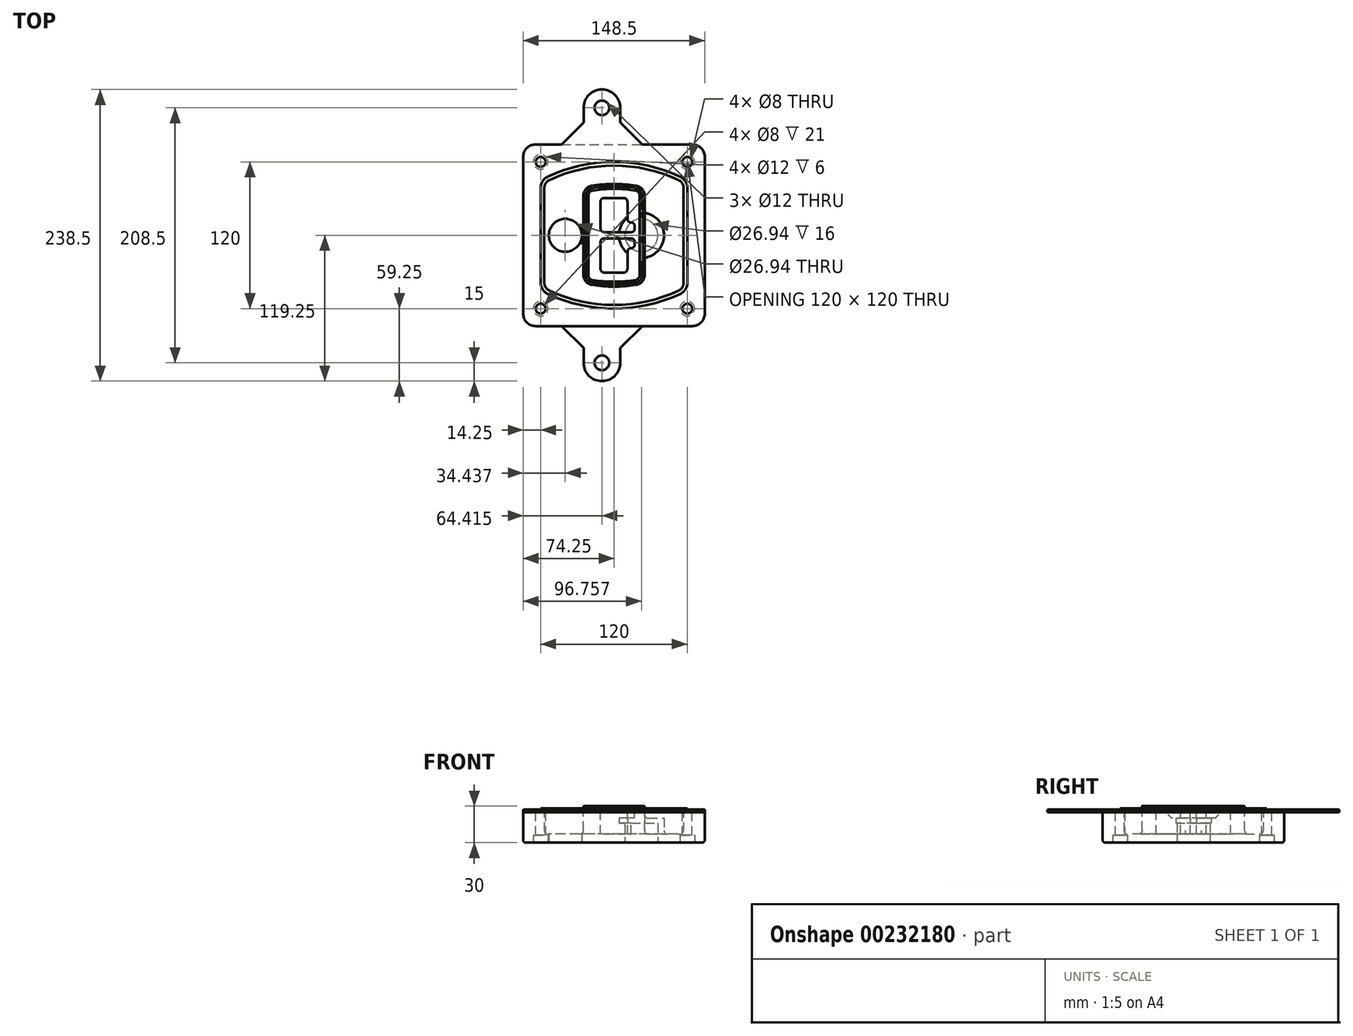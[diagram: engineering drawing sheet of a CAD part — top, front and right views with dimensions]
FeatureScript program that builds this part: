
annotation { "Feature Type Name" : "Feature", "Feature Type Description" : "" }
export const myFeature = defineFeature(function(context is Context, id is Id, definition is map)
    precondition{}
    {
        {
            var Q0;
            Q0=qCreatedBy(makeId("Top.planeOp"),FACE);
            var sketch = newSketch(context, id + "F0", { "sketchPlane" : qUnion([Q0])});
            skPoint(sketch, "E0.rect.middle", {"position": v(0, 0) * mm});
            skLineSegment(sketch, "E1.bottom", {"start": v(-64.25, -74.25) * mm, "end": v(64.25, -74.25) * mm});
            skLineSegment(sketch, "E1.top", {"start": v(-64.25, 74.25) * mm, "end": v(64.25, 74.25) * mm});
            skLineSegment(sketch, "E1.left", {"start": v(-74.25, -64.25) * mm, "end": v(-74.25, 64.25) * mm});
            skLineSegment(sketch, "E1.right", {"start": v(74.25, -64.25) * mm, "end": v(74.25, 64.25) * mm});
            skLineSegment(sketch, "E2", {"start": v(-74.25, 74.25) * mm, "end": v(74.25, -74.25) * mm, "construction": true});
            skLineSegment(sketch, "E3", {"start": v(74.25, 74.25) * mm, "end": v(-74.25, -74.25) * mm, "construction": true});
            skCircle(sketch, "E4", {"center": v(-60, 60) * mm, "radius": 4 * mm});
            skCircle(sketch, "E5", {"center": v(60, 60) * mm, "radius": 4 * mm});
            skCircle(sketch, "E6", {"center": v(60, -60) * mm, "radius": 4 * mm});
            skCircle(sketch, "E7", {"center": v(-60, -60) * mm, "radius": 4 * mm});
            skLineSegment(sketch, "E8", {"start": v(-60, 60) * mm, "end": v(60, 60) * mm, "construction": true});
            skLineSegment(sketch, "E9", {"start": v(60, 60) * mm, "end": v(60, -60) * mm, "construction": true});
            skLineSegment(sketch, "E10", {"start": v(60, -60) * mm, "end": v(-60, -60) * mm, "construction": true});
            skLineSegment(sketch, "E11", {"start": v(-60, -60) * mm, "end": v(-60, 60) * mm, "construction": true});
            skLineSegment(sketch, "E12", {"start": v(-60, 38.83) * mm, "end": v(-60, -38.83) * mm});
            skLineSegment(sketch, "E13", {"start": v(60, 38.83) * mm, "end": v(60, -38.83) * mm});
            skArc(sketch, "E14", {"start": v(54.26, 47.88) * mm, "mid": v(0, 60) * mm, "end": v(-54.26, 47.88) * mm});
            skArc(sketch, "E15", {"start": v(-54.26, -47.88) * mm, "mid": v(0, -60) * mm, "end": v(54.26, -47.88) * mm});
            skLineSegment(sketch, "E16", {"start": v(-60, 0) * mm, "end": v(60, 0) * mm, "construction": true});
            skPoint(sketch, "E17.visualSharp", {"position": v(-60, -45) * mm});
            skArc(sketch, "E17.filletArc", {"start": v(-60, -38.83) * mm, "mid": v(-58.44, -44.2) * mm, "end": v(-54.26, -47.88) * mm});
            skPoint(sketch, "E18.visualSharp", {"position": v(-60, 45) * mm});
            skArc(sketch, "E18.filletArc", {"start": v(-54.26, 47.88) * mm, "mid": v(-58.44, 44.2) * mm, "end": v(-60, 38.83) * mm});
            skPoint(sketch, "E19.visualSharp", {"position": v(60, 45) * mm});
            skArc(sketch, "E19.filletArc", {"start": v(60, 38.83) * mm, "mid": v(58.44, 44.2) * mm, "end": v(54.26, 47.88) * mm});
            skPoint(sketch, "E20.visualSharp", {"position": v(60, -45) * mm});
            skArc(sketch, "E20.filletArc", {"start": v(54.26, -47.88) * mm, "mid": v(58.44, -44.2) * mm, "end": v(60, -38.83) * mm});
            skPoint(sketch, "E21.visualSharp", {"position": v(-74.25, 74.25) * mm});
            skArc(sketch, "E21.filletArc", {"start": v(-64.25, 74.25) * mm, "mid": v(-71.32, 71.32) * mm, "end": v(-74.25, 64.25) * mm});
            skPoint(sketch, "E22.visualSharp", {"position": v(74.25, 74.25) * mm});
            skArc(sketch, "E22.filletArc", {"start": v(74.25, 64.25) * mm, "mid": v(71.32, 71.32) * mm, "end": v(64.25, 74.25) * mm});
            skPoint(sketch, "E23.visualSharp", {"position": v(74.25, -74.25) * mm});
            skArc(sketch, "E23.filletArc", {"start": v(64.25, -74.25) * mm, "mid": v(71.32, -71.32) * mm, "end": v(74.25, -64.25) * mm});
            skPoint(sketch, "E24.visualSharp", {"position": v(-74.25, -74.25) * mm});
            skArc(sketch, "E24.filletArc", {"start": v(-74.25, -64.25) * mm, "mid": v(-71.32, -71.32) * mm, "end": v(-64.25, -74.25) * mm});
            skArc(sketch, "E25.0", {"start": v(57, 38.83) * mm, "mid": v(55.9, 42.58) * mm, "end": v(52.98, 45.17) * mm});
            skLineSegment(sketch, "E25.1", {"start": v(57, 38.83) * mm, "end": v(57, -38.83) * mm});
            skArc(sketch, "E25.2", {"start": v(52.98, -45.17) * mm, "mid": v(55.9, -42.58) * mm, "end": v(57, -38.83) * mm});
            skArc(sketch, "E25.3", {"start": v(-52.98, -45.17) * mm, "mid": v(0, -57) * mm, "end": v(52.98, -45.17) * mm});
            skArc(sketch, "E25.4", {"start": v(-57, -38.83) * mm, "mid": v(-55.9, -42.58) * mm, "end": v(-52.98, -45.17) * mm});
            skArc(sketch, "E25.5", {"start": v(52.98, 45.17) * mm, "mid": v(0, 57) * mm, "end": v(-52.98, 45.17) * mm});
            skLineSegment(sketch, "E25.6", {"start": v(-57, 38.83) * mm, "end": v(-57, -38.83) * mm});
            skArc(sketch, "E25.7", {"start": v(-52.98, 45.17) * mm, "mid": v(-55.9, 42.58) * mm, "end": v(-57, 38.83) * mm});
            skArc(sketch, "E26.0", {"start": v(-55.96, 51.5) * mm, "mid": v(-61.82, 46.33) * mm, "end": v(-64, 38.83) * mm});
            skArc(sketch, "E26.1", {"start": v(55.96, 51.5) * mm, "mid": v(0, 64) * mm, "end": v(-55.96, 51.5) * mm});
            skArc(sketch, "E26.2", {"start": v(64, 38.83) * mm, "mid": v(61.82, 46.33) * mm, "end": v(55.96, 51.5) * mm});
            skLineSegment(sketch, "E26.3", {"start": v(64, 38.83) * mm, "end": v(64, -38.83) * mm});
            skArc(sketch, "E26.4", {"start": v(55.96, -51.5) * mm, "mid": v(61.82, -46.33) * mm, "end": v(64, -38.83) * mm});
            skLineSegment(sketch, "E26.5", {"start": v(-64, 38.83) * mm, "end": v(-64, -38.83) * mm});
            skArc(sketch, "E26.6", {"start": v(-55.96, -51.5) * mm, "mid": v(0, -64) * mm, "end": v(55.96, -51.5) * mm});
            skArc(sketch, "E26.7", {"start": v(-64, -38.83) * mm, "mid": v(-61.82, -46.33) * mm, "end": v(-55.96, -51.5) * mm});
            skSolve(sketch);
        }
        {
            var Q0;
            Q0=makeQuery(id+"F0.imprint","IMPRINT",FACE,{"disambiguationData":[TD([[makeQuery(id+"F0.imprint","IMPRINT",EDGE,{"derivedFrom":sQuery(id+"F0.wireOp",EDGE,"E1.bottom")}),1.0]])]});
            var Q1;
            Q1=makeQuery(id+"F0.imprint","IMPRINT",FACE,{"disambiguationData":[TD([[makeQuery(id+"F0.imprint","IMPRINT",EDGE,{"derivedFrom":sQuery(id+"F0.wireOp",EDGE,"E12")}),1.0]])]});
            var Q2;
            Q2=makeQuery(id+"F0.imprint","IMPRINT",FACE,{"disambiguationData":[TD([[makeQuery(id+"F0.imprint","IMPRINT",EDGE,{"derivedFrom":sQuery(id+"F0.wireOp",EDGE,"E25.0")}),1.0]])]});
            var Q3;
            Q3=makeQuery(id+"F0.imprint","IMPRINT",FACE,{"disambiguationData":[TD([[makeQuery(id+"F0.imprint","IMPRINT",EDGE,{"derivedFrom":sQuery(id+"F0.wireOp",EDGE,"E12")}),-1.0]])]});
            extrude(context, id + "F1", {"entities" : qUnion([Q0, Q1, Q2, Q3]), "oppositeDirection" : true, "depth" : 25 * mm});
        }
        {
            var Q0;
            Q0=makeQuery(id+"F0.imprint","IMPRINT",FACE,{"disambiguationData":[TD([[makeQuery(id+"F0.imprint","IMPRINT",EDGE,{"derivedFrom":sQuery(id+"F0.wireOp",EDGE,"E12")}),1.0]])]});
            extrude(context, id + "F2", {"entities" : qUnion([Q0]), "operationType" : NewBodyOperationType.ADD, "depth" : 3 * mm});
        }
        {
            var Q0;
            Q0=makeQuery(id+"F0.imprint","IMPRINT",FACE,{"disambiguationData":[TD([[makeQuery(id+"F0.imprint","IMPRINT",EDGE,{"derivedFrom":sQuery(id+"F0.wireOp",EDGE,"E25.0")}),1.0]])]});
            extrude(context, id + "F3", {"entities" : qUnion([Q0]), "operationType" : NewBodyOperationType.REMOVE, "oppositeDirection" : true, "depth" : 18 * mm});
        }
        {
            var Q0;
            Q0=makeQuery(id+"F2.opExtrude","CAP_FACE",FACE,{"disambiguationData":[OSD([sQuery(id+"F0.wireOp",EDGE,"E12"),sQuery(id+"F0.wireOp",EDGE,"E13"),sQuery(id+"F0.wireOp",EDGE,"E14"),sQuery(id+"F0.wireOp",EDGE,"E15"),sQuery(id+"F0.wireOp",EDGE,"E17.filletArc"),sQuery(id+"F0.wireOp",EDGE,"E18.filletArc"),sQuery(id+"F0.wireOp",EDGE,"E19.filletArc"),sQuery(id+"F0.wireOp",EDGE,"E20.filletArc"),sQuery(id+"F0.wireOp",EDGE,"E25.0"),sQuery(id+"F0.wireOp",EDGE,"E25.1"),sQuery(id+"F0.wireOp",EDGE,"E25.2"),sQuery(id+"F0.wireOp",EDGE,"E25.3"),sQuery(id+"F0.wireOp",EDGE,"E25.4"),sQuery(id+"F0.wireOp",EDGE,"E25.5"),sQuery(id+"F0.wireOp",EDGE,"E25.6"),sQuery(id+"F0.wireOp",EDGE,"E25.7")])],"isStart":false});
            var sketch = newSketch(context, id + "F4", { "sketchPlane" : qUnion([Q0])});
            skArc(sketch, "E27.0", {"start": v(-18.34, -40.45) * mm, "mid": v(0, -42) * mm, "end": v(18.34, -40.45) * mm});
            skArc(sketch, "E28.0", {"start": v(18.34, 40.45) * mm, "mid": v(0, 42) * mm, "end": v(-18.34, 40.45) * mm});
            skLineSegment(sketch, "E29", {"start": v(-25, 32.57) * mm, "end": v(-25, -32.57) * mm});
            skLineSegment(sketch, "E30", {"start": v(25, 32.57) * mm, "end": v(25, -32.57) * mm});
            skLineSegment(sketch, "E31", {"start": v(-25, 39.1) * mm, "end": v(25, 39.1) * mm, "construction": true});
            skLineSegment(sketch, "E32", {"start": v(-25, -39.1) * mm, "end": v(25, -39.1) * mm, "construction": true});
            skPoint(sketch, "E33.visualSharp", {"position": v(-25, 39.1) * mm});
            skArc(sketch, "E33.filletArc", {"start": v(-18.34, 40.45) * mm, "mid": v(-23.11, 37.73) * mm, "end": v(-25, 32.57) * mm});
            skPoint(sketch, "E34.visualSharp", {"position": v(25, 39.1) * mm});
            skArc(sketch, "E34.filletArc", {"start": v(25, 32.57) * mm, "mid": v(23.11, 37.73) * mm, "end": v(18.34, 40.45) * mm});
            skPoint(sketch, "E35.visualSharp", {"position": v(25, -39.1) * mm});
            skArc(sketch, "E35.filletArc", {"start": v(18.34, -40.45) * mm, "mid": v(23.11, -37.73) * mm, "end": v(25, -32.57) * mm});
            skPoint(sketch, "E36.visualSharp", {"position": v(-25, -39.1) * mm});
            skArc(sketch, "E36.filletArc", {"start": v(-25, -32.57) * mm, "mid": v(-23.11, -37.73) * mm, "end": v(-18.34, -40.45) * mm});
            skArc(sketch, "E37.0", {"start": v(52.98, 45.17) * mm, "mid": v(0, 57) * mm, "end": v(-52.98, 45.17) * mm});
            skArc(sketch, "E37.1", {"start": v(-52.98, 45.17) * mm, "mid": v(-55.9, 42.58) * mm, "end": v(-57, 38.83) * mm});
            skLineSegment(sketch, "E37.2", {"start": v(-57, 38.83) * mm, "end": v(-57, -38.83) * mm});
            skArc(sketch, "E37.3", {"start": v(-57, -38.83) * mm, "mid": v(-55.9, -42.58) * mm, "end": v(-52.98, -45.17) * mm});
            skArc(sketch, "E37.4", {"start": v(-52.98, -45.17) * mm, "mid": v(0, -57) * mm, "end": v(52.98, -45.17) * mm});
            skArc(sketch, "E37.5", {"start": v(52.98, -45.17) * mm, "mid": v(55.9, -42.58) * mm, "end": v(57, -38.83) * mm});
            skLineSegment(sketch, "E37.6", {"start": v(57, 38.83) * mm, "end": v(57, -38.83) * mm});
            skArc(sketch, "E37.7", {"start": v(57, 38.83) * mm, "mid": v(55.9, 42.58) * mm, "end": v(52.98, 45.17) * mm});
            skLineSegment(sketch, "E38.0", {"start": v(23, 32.57) * mm, "end": v(23, -32.57) * mm});
            skArc(sketch, "E38.1", {"start": v(18, -38.48) * mm, "mid": v(21.58, -36.44) * mm, "end": v(23, -32.57) * mm});
            skArc(sketch, "E38.2", {"start": v(-18, -38.48) * mm, "mid": v(0, -40) * mm, "end": v(18, -38.48) * mm});
            skArc(sketch, "E38.3", {"start": v(-23, -32.57) * mm, "mid": v(-21.58, -36.44) * mm, "end": v(-18, -38.48) * mm});
            skLineSegment(sketch, "E38.4", {"start": v(-23, 32.57) * mm, "end": v(-23, -32.57) * mm});
            skArc(sketch, "E38.5", {"start": v(23, 32.57) * mm, "mid": v(21.58, 36.44) * mm, "end": v(18, 38.48) * mm});
            skArc(sketch, "E38.6", {"start": v(-18, 38.48) * mm, "mid": v(-21.58, 36.44) * mm, "end": v(-23, 32.57) * mm});
            skArc(sketch, "E38.7", {"start": v(18, 38.48) * mm, "mid": v(0, 40) * mm, "end": v(-18, 38.48) * mm});
            skArc(sketch, "E39.0", {"start": v(21, 32.57) * mm, "mid": v(20.06, 35.15) * mm, "end": v(17.67, 36.5) * mm});
            skLineSegment(sketch, "E39.1", {"start": v(21, 32.57) * mm, "end": v(21, -32.57) * mm});
            skArc(sketch, "E39.2", {"start": v(17.67, -36.5) * mm, "mid": v(20.06, -35.15) * mm, "end": v(21, -32.57) * mm});
            skArc(sketch, "E39.3", {"start": v(-17.67, -36.5) * mm, "mid": v(0, -38) * mm, "end": v(17.67, -36.5) * mm});
            skArc(sketch, "E39.4", {"start": v(-21, -32.57) * mm, "mid": v(-20.06, -35.15) * mm, "end": v(-17.67, -36.5) * mm});
            skArc(sketch, "E39.5", {"start": v(17.67, 36.5) * mm, "mid": v(0, 38) * mm, "end": v(-17.67, 36.5) * mm});
            skLineSegment(sketch, "E39.6", {"start": v(-21, 32.57) * mm, "end": v(-21, -32.57) * mm});
            skArc(sketch, "E39.7", {"start": v(-17.67, 36.5) * mm, "mid": v(-20.06, 35.15) * mm, "end": v(-21, 32.57) * mm});
            skLineSegment(sketch, "E40", {"start": v(-25, 0) * mm, "end": v(25, 0) * mm, "construction": true});
            skLineSegment(sketch, "E41", {"start": v(-11, 5.5) * mm, "end": v(-11, 27.5) * mm});
            skLineSegment(sketch, "E42", {"start": v(-8, 30.5) * mm, "end": v(8, 30.5) * mm});
            skLineSegment(sketch, "E43", {"start": v(11, 27.5) * mm, "end": v(11, 13.5) * mm});
            skLineSegment(sketch, "E44", {"start": v(14, 10.5) * mm, "end": v(14, 10.5) * mm});
            skLineSegment(sketch, "E45", {"start": v(17, 7.5) * mm, "end": v(17, 5.5) * mm});
            skLineSegment(sketch, "E46", {"start": v(14, 2.5) * mm, "end": v(-8, 2.5) * mm});
            skPoint(sketch, "E47.visualSharp", {"position": v(-11, 30.5) * mm});
            skArc(sketch, "E47.filletArc", {"start": v(-8, 30.5) * mm, "mid": v(-10.12, 29.62) * mm, "end": v(-11, 27.5) * mm});
            skPoint(sketch, "E48.visualSharp", {"position": v(11, 30.5) * mm});
            skArc(sketch, "E48.filletArc", {"start": v(11, 27.5) * mm, "mid": v(10.12, 29.62) * mm, "end": v(8, 30.5) * mm});
            skPoint(sketch, "E49.visualSharp", {"position": v(11, 10.5) * mm});
            skArc(sketch, "E49.filletArc", {"start": v(11, 13.5) * mm, "mid": v(11.88, 11.38) * mm, "end": v(14, 10.5) * mm});
            skPoint(sketch, "E50.visualSharp", {"position": v(17, 10.5) * mm});
            skArc(sketch, "E50.filletArc", {"start": v(17, 7.5) * mm, "mid": v(16.12, 9.62) * mm, "end": v(14, 10.5) * mm});
            skPoint(sketch, "E51.visualSharp", {"position": v(17, 2.5) * mm});
            skArc(sketch, "E51.filletArc", {"start": v(14, 2.5) * mm, "mid": v(16.12, 3.38) * mm, "end": v(17, 5.5) * mm});
            skPoint(sketch, "E52.visualSharp", {"position": v(-11, 2.5) * mm});
            skArc(sketch, "E52.filletArc", {"start": v(-11, 5.5) * mm, "mid": v(-10.12, 3.38) * mm, "end": v(-8, 2.5) * mm});
            skLineSegment(sketch, "E53.0.MirrorCS", {"start": v(14, -2.5) * mm, "end": v(-8, -2.5) * mm});
            skArc(sketch, "E54.0.MirrorCS", {"start": v(-11, -5.5) * mm, "mid": v(-10.12, -3.38) * mm, "end": v(-8, -2.5) * mm});
            skLineSegment(sketch, "E55.0.MirrorCS", {"start": v(-11, -5.5) * mm, "end": v(-11, -27.5) * mm});
            skArc(sketch, "E56.0.MirrorCS", {"start": v(-8, -30.5) * mm, "mid": v(-10.12, -29.62) * mm, "end": v(-11, -27.5) * mm});
            skLineSegment(sketch, "E57.0.MirrorCS", {"start": v(-8, -30.5) * mm, "end": v(8, -30.5) * mm});
            skArc(sketch, "E58.0.MirrorCS", {"start": v(11, -27.5) * mm, "mid": v(10.12, -29.62) * mm, "end": v(8, -30.5) * mm});
            skLineSegment(sketch, "E59.0.MirrorCS", {"start": v(11, -27.5) * mm, "end": v(11, -13.5) * mm});
            skArc(sketch, "E60.0.MirrorCS", {"start": v(11, -13.5) * mm, "mid": v(11.88, -11.38) * mm, "end": v(14, -10.5) * mm});
            skArc(sketch, "E61.0.MirrorCS", {"start": v(17, -7.5) * mm, "mid": v(16.12, -9.62) * mm, "end": v(14, -10.5) * mm});
            skLineSegment(sketch, "E62.0.MirrorCS", {"start": v(17, -7.5) * mm, "end": v(17, -5.5) * mm});
            skArc(sketch, "E63.0.MirrorCS", {"start": v(14, -2.5) * mm, "mid": v(16.12, -3.38) * mm, "end": v(17, -5.5) * mm});
            skSolve(sketch);
        }
        {
            var Q0;
            Q0=makeQuery(id+"F4.imprint","IMPRINT",FACE,{"disambiguationData":[TD([[makeQuery(id+"F4.imprint","IMPRINT",EDGE,{"derivedFrom":sQuery(id+"F4.wireOp",EDGE,"E27.0")}),1.0]])]});
            var Q1;
            Q1=makeQuery(id+"F4.imprint","IMPRINT",FACE,{"disambiguationData":[TD([[makeQuery(id+"F4.imprint","IMPRINT",EDGE,{"derivedFrom":sQuery(id+"F4.wireOp",EDGE,"E38.0")}),-1.0]])]});
            var Q2;
            Q2=makeQuery(id+"F4.imprint","IMPRINT",FACE,{"disambiguationData":[TD([[makeQuery(id+"F4.imprint","IMPRINT",EDGE,{"derivedFrom":sQuery(id+"F4.wireOp",EDGE,"E39.0")}),1.0]])]});
            extrude(context, id + "F5", {"entities" : qUnion([Q0, Q1, Q2]), "operationType" : NewBodyOperationType.ADD, "endBound" : BoundingType.UP_TO_NEXT, "oppositeDirection" : true, "depth" : 25 * mm});
        }
        {
            var Q0;
            Q0=makeQuery(id+"F4.imprint","IMPRINT",FACE,{"disambiguationData":[TD([[makeQuery(id+"F4.imprint","IMPRINT",EDGE,{"derivedFrom":sQuery(id+"F4.wireOp",EDGE,"E38.0")}),-1.0]])]});
            extrude(context, id + "F6", {"entities" : qUnion([Q0]), "operationType" : NewBodyOperationType.REMOVE, "oppositeDirection" : true, "depth" : 2 * mm});
        }
        {
            var Q0;
            Q0=makeQuery(id+"F1.opExtrude","CAP_FACE",FACE,{"disambiguationData":[OSD([sQuery(id+"F0.wireOp",EDGE,"E1.bottom"),sQuery(id+"F0.wireOp",EDGE,"E1.top"),sQuery(id+"F0.wireOp",EDGE,"E1.left"),sQuery(id+"F0.wireOp",EDGE,"E1.right"),sQuery(id+"F0.wireOp",EDGE,"E4"),sQuery(id+"F0.wireOp",EDGE,"E5"),sQuery(id+"F0.wireOp",EDGE,"E6"),sQuery(id+"F0.wireOp",EDGE,"E7"),sQuery(id+"F0.wireOp",EDGE,"E21.filletArc"),sQuery(id+"F0.wireOp",EDGE,"E22.filletArc"),sQuery(id+"F0.wireOp",EDGE,"E23.filletArc"),sQuery(id+"F0.wireOp",EDGE,"E24.filletArc")])],"isStart":false});
            var sketch = newSketch(context, id + "F7", { "sketchPlane" : qUnion([Q0])});
            skCircle(sketch, "E64", {"center": v(22.5, 0) * mm, "radius": 13.47 * mm});
            skCircle(sketch, "E65", {"center": v(-39.81, 0) * mm, "radius": 13.47 * mm});
            skLineSegment(sketch, "E66", {"start": v(74.25, 0) * mm, "end": v(-74.25, 0) * mm});
            skCircle(sketch, "E67", {"center": v(22.5, 0) * mm, "radius": 18.47 * mm});
            skCircle(sketch, "E68", {"center": v(60, -60) * mm, "radius": 6 * mm});
            skCircle(sketch, "E69", {"center": v(-60, -60) * mm, "radius": 6 * mm});
            skCircle(sketch, "E70", {"center": v(-60, 60) * mm, "radius": 6 * mm});
            skCircle(sketch, "E71", {"center": v(60, 60) * mm, "radius": 6 * mm});
            skSolve(sketch);
        }
        {
            var Q0;
            {var subQ1=sQuery(id+"F7.wireOp",EDGE,"E66");var subQ4=sQuery(id+"F7.wireOp",EDGE,"E64");var subQ6=makeQuery(id+"F7.imprint","INTERSECT",VERTEX,{"disambiguationData":[OD(0.0)],"derivedFrom":[subQ4,subQ1]});Q0=makeQuery(id+"F7.imprint","IMPRINT",FACE,{"disambiguationData":[TD([[makeQuery(id+"F7.imprint","IMPRINT",EDGE,{"disambiguationData":[TD([[subQ6,-1.0]])],"derivedFrom":subQ4}),-1.0]])]});}
            var Q1;
            {var subQ0=sQuery(id+"F7.wireOp",EDGE,"E66");var subQ1=sQuery(id+"F7.wireOp",EDGE,"E64");var subQ3=makeQuery(id+"F7.imprint","INTERSECT",VERTEX,{"disambiguationData":[OD(0.0)],"derivedFrom":[subQ1,subQ0]});Q1=makeQuery(id+"F7.imprint","IMPRINT",FACE,{"disambiguationData":[TD([[makeQuery(id+"F7.imprint","IMPRINT",EDGE,{"disambiguationData":[TD([[subQ3,-1.0]])],"derivedFrom":subQ1}),1.0]])]});}
            var Q2;
            {var subQ0=sQuery(id+"F7.wireOp",EDGE,"E66");var subQ1=sQuery(id+"F7.wireOp",EDGE,"E64");var subQ3=makeQuery(id+"F7.imprint","INTERSECT",VERTEX,{"disambiguationData":[OD(0.0)],"derivedFrom":[subQ1,subQ0]});Q2=makeQuery(id+"F7.imprint","IMPRINT",FACE,{"disambiguationData":[TD([[makeQuery(id+"F7.imprint","IMPRINT",EDGE,{"disambiguationData":[TD([[subQ3,1.0]])],"derivedFrom":subQ1}),1.0]])]});}
            var Q3;
            {var subQ1=sQuery(id+"F7.wireOp",EDGE,"E66");var subQ4=sQuery(id+"F7.wireOp",EDGE,"E64");var subQ6=makeQuery(id+"F7.imprint","INTERSECT",VERTEX,{"disambiguationData":[OD(0.0)],"derivedFrom":[subQ4,subQ1]});Q3=makeQuery(id+"F7.imprint","IMPRINT",FACE,{"disambiguationData":[TD([[makeQuery(id+"F7.imprint","IMPRINT",EDGE,{"disambiguationData":[TD([[subQ6,1.0]])],"derivedFrom":subQ4}),-1.0]])]});}
            extrude(context, id + "F8", {"entities" : qUnion([Q0, Q1, Q2, Q3]), "operationType" : NewBodyOperationType.ADD, "oppositeDirection" : true, "depth" : 20 * mm});
        }
        {
            var Q0;
            {var subQ0=sQuery(id+"F7.wireOp",EDGE,"E66");var subQ1=sQuery(id+"F7.wireOp",EDGE,"E64");var subQ3=makeQuery(id+"F7.imprint","INTERSECT",VERTEX,{"disambiguationData":[OD(0.0)],"derivedFrom":[subQ1,subQ0]});Q0=makeQuery(id+"F7.imprint","IMPRINT",FACE,{"disambiguationData":[TD([[makeQuery(id+"F7.imprint","IMPRINT",EDGE,{"disambiguationData":[TD([[subQ3,-1.0]])],"derivedFrom":subQ1}),1.0]])]});}
            var Q1;
            {var subQ0=sQuery(id+"F7.wireOp",EDGE,"E66");var subQ1=sQuery(id+"F7.wireOp",EDGE,"E64");var subQ3=makeQuery(id+"F7.imprint","INTERSECT",VERTEX,{"disambiguationData":[OD(0.0)],"derivedFrom":[subQ1,subQ0]});Q1=makeQuery(id+"F7.imprint","IMPRINT",FACE,{"disambiguationData":[TD([[makeQuery(id+"F7.imprint","IMPRINT",EDGE,{"disambiguationData":[TD([[subQ3,1.0]])],"derivedFrom":subQ1}),1.0]])]});}
            extrude(context, id + "F9", {"entities" : qUnion([Q0, Q1]), "operationType" : NewBodyOperationType.REMOVE, "oppositeDirection" : true, "depth" : 16 * mm});
        }
        {
            var Q0;
            {var subQ0=sQuery(id+"F7.wireOp",EDGE,"E66");var subQ1=sQuery(id+"F7.wireOp",EDGE,"E65");var subQ3=makeQuery(id+"F7.imprint","INTERSECT",VERTEX,{"disambiguationData":[OD(0.0)],"derivedFrom":[subQ1,subQ0]});Q0=makeQuery(id+"F7.imprint","IMPRINT",FACE,{"disambiguationData":[TD([[makeQuery(id+"F7.imprint","IMPRINT",EDGE,{"disambiguationData":[TD([[subQ3,-1.0]])],"derivedFrom":subQ1}),1.0]])]});}
            var Q1;
            {var subQ0=sQuery(id+"F7.wireOp",EDGE,"E66");var subQ1=sQuery(id+"F7.wireOp",EDGE,"E65");var subQ3=makeQuery(id+"F7.imprint","INTERSECT",VERTEX,{"disambiguationData":[OD(0.0)],"derivedFrom":[subQ1,subQ0]});Q1=makeQuery(id+"F7.imprint","IMPRINT",FACE,{"disambiguationData":[TD([[makeQuery(id+"F7.imprint","IMPRINT",EDGE,{"disambiguationData":[TD([[subQ3,1.0]])],"derivedFrom":subQ1}),1.0]])]});}
            extrude(context, id + "F10", {"entities" : qUnion([Q0, Q1]), "operationType" : NewBodyOperationType.REMOVE, "oppositeDirection" : true, "depth" : 25 * mm});
        }
        {
            var Q0;
            Q0=makeQuery(id+"F7.imprint","IMPRINT",FACE,{"disambiguationData":[TD([[makeQuery(id+"F7.imprint","IMPRINT",EDGE,{"derivedFrom":sQuery(id+"F7.wireOp",EDGE,"E68")}),1.0]])]});
            var Q1;
            Q1=makeQuery(id+"F7.imprint","IMPRINT",FACE,{"disambiguationData":[TD([[makeQuery(id+"F7.imprint","IMPRINT",EDGE,{"derivedFrom":makeQuery(id+"F1.opExtrude","CAP_EDGE",EDGE,{"disambiguationData":[OSD([sQuery(id+"F0.wireOp",EDGE,"E5")])],"isStart":false})}),-1.0]])]});
            var Q2;
            Q2=makeQuery(id+"F7.imprint","IMPRINT",FACE,{"disambiguationData":[TD([[makeQuery(id+"F7.imprint","IMPRINT",EDGE,{"derivedFrom":sQuery(id+"F7.wireOp",EDGE,"E69")}),1.0]])]});
            var Q3;
            Q3=makeQuery(id+"F7.imprint","IMPRINT",FACE,{"disambiguationData":[TD([[makeQuery(id+"F7.imprint","IMPRINT",EDGE,{"derivedFrom":makeQuery(id+"F1.opExtrude","CAP_EDGE",EDGE,{"disambiguationData":[OSD([sQuery(id+"F0.wireOp",EDGE,"E4")])],"isStart":false})}),-1.0]])]});
            var Q4;
            Q4=makeQuery(id+"F7.imprint","IMPRINT",FACE,{"disambiguationData":[TD([[makeQuery(id+"F7.imprint","IMPRINT",EDGE,{"derivedFrom":sQuery(id+"F7.wireOp",EDGE,"E70")}),1.0]])]});
            var Q5;
            Q5=makeQuery(id+"F7.imprint","IMPRINT",FACE,{"disambiguationData":[TD([[makeQuery(id+"F7.imprint","IMPRINT",EDGE,{"derivedFrom":makeQuery(id+"F1.opExtrude","CAP_EDGE",EDGE,{"disambiguationData":[OSD([sQuery(id+"F0.wireOp",EDGE,"E7")])],"isStart":false})}),-1.0]])]});
            var Q6;
            Q6=makeQuery(id+"F7.imprint","IMPRINT",FACE,{"disambiguationData":[TD([[makeQuery(id+"F7.imprint","IMPRINT",EDGE,{"derivedFrom":sQuery(id+"F7.wireOp",EDGE,"E71")}),1.0]])]});
            var Q7;
            Q7=makeQuery(id+"F7.imprint","IMPRINT",FACE,{"disambiguationData":[TD([[makeQuery(id+"F7.imprint","IMPRINT",EDGE,{"derivedFrom":makeQuery(id+"F1.opExtrude","CAP_EDGE",EDGE,{"disambiguationData":[OSD([sQuery(id+"F0.wireOp",EDGE,"E6")])],"isStart":false})}),-1.0]])]});
            extrude(context, id + "F11", {"entities" : qUnion([Q0, Q1, Q2, Q3, Q4, Q5, Q6, Q7]), "operationType" : NewBodyOperationType.REMOVE, "oppositeDirection" : true, "depth" : 6 * mm});
        }
        {
            var Q0;
            Q0=makeQuery(id+"F9.boolean.opBoolean","COPY",FACE,{"derivedFrom":makeQuery(id+"F9.opExtrude","CAP_FACE",FACE,{"disambiguationData":[OSD([sQuery(id+"F7.wireOp",EDGE,"E64")])],"isStart":false})});
            var sketch = newSketch(context, id + "F12", { "sketchPlane" : qUnion([Q0])});
            skArc(sketch, "E72.0", {"start": v(11, 14.45) * mm, "mid": v(6.45, 9.13) * mm, "end": v(4.2, 2.5) * mm});
            skArc(sketch, "E72.1", {"start": v(4.2, -2.5) * mm, "mid": v(6.45, -9.13) * mm, "end": v(11, -14.45) * mm});
            skLineSegment(sketch, "E73", {"start": v(4.2, -2.5) * mm, "end": v(14, -2.5) * mm});
            skLineSegment(sketch, "E74.0", {"start": v(14, 2.5) * mm, "end": v(4.2, 2.5) * mm});
            skArc(sketch, "E74.1", {"start": v(14, 2.5) * mm, "mid": v(16.12, 3.38) * mm, "end": v(17, 5.5) * mm});
            skLineSegment(sketch, "E74.2", {"start": v(17, 7.5) * mm, "end": v(17, 5.5) * mm});
            skArc(sketch, "E74.3", {"start": v(17, 7.5) * mm, "mid": v(16.12, 9.62) * mm, "end": v(14, 10.5) * mm});
            skArc(sketch, "E74.4", {"start": v(11, 13.5) * mm, "mid": v(11.88, 11.38) * mm, "end": v(14, 10.5) * mm});
            skLineSegment(sketch, "E74.5", {"start": v(11, 14.45) * mm, "end": v(11, 13.5) * mm});
            skLineSegment(sketch, "E74.7", {"start": v(14, -2.5) * mm, "end": v(4.2, -2.5) * mm});
            skArc(sketch, "E74.8", {"start": v(14, -2.5) * mm, "mid": v(16.12, -3.38) * mm, "end": v(17, -5.5) * mm});
            skLineSegment(sketch, "E74.9", {"start": v(17, -7.5) * mm, "end": v(17, -5.5) * mm});
            skArc(sketch, "E74.10", {"start": v(17, -7.5) * mm, "mid": v(16.12, -9.62) * mm, "end": v(14, -10.5) * mm});
            skArc(sketch, "E74.11", {"start": v(11, -13.5) * mm, "mid": v(11.88, -11.38) * mm, "end": v(14, -10.5) * mm});
            skLineSegment(sketch, "E74.12", {"start": v(11, -14.45) * mm, "end": v(11, -13.5) * mm});
            skPoint(sketch, "E75.orphan", {"position": v(11, -27.5) * mm});
            skPoint(sketch, "E76.orphan", {"position": v(-8, -2.5) * mm});
            skPoint(sketch, "E77.orphan", {"position": v(-8, 2.5) * mm});
            skPoint(sketch, "E78.orphan", {"position": v(11, 27.5) * mm});
            skSolve(sketch);
        }
        {
            var Q0;
            {var subQ7=sQuery(id+"F12.wireOp",EDGE,"E72.0");var subQ14=sQuery(id+"F12.wireOp",EDGE,"E72.1");var subQ16=sQuery(id+"F12.wireOp",EDGE,"E74.1");var subQ18=sQuery(id+"F12.wireOp",EDGE,"E74.8");Q0=qUnion([makeQuery(id+"F12.imprint","IMPRINT",FACE,{"disambiguationData":[TD([[makeQuery(id+"F12.imprint","IMPRINT",EDGE,{"derivedFrom":subQ7}),1.0]])]}),makeQuery(id+"F12.imprint","IMPRINT",FACE,{"disambiguationData":[TD([[makeQuery(id+"F12.imprint","IMPRINT",EDGE,{"derivedFrom":subQ14}),1.0]])]}),makeQuery(id+"F12.imprint","IMPRINT",FACE,{"disambiguationData":[TD([[makeQuery(id+"F12.imprint","IMPRINT",EDGE,{"derivedFrom":subQ16}),1.0]])]}),makeQuery(id+"F12.imprint","IMPRINT",FACE,{"disambiguationData":[TD([[makeQuery(id+"F12.imprint","IMPRINT",EDGE,{"derivedFrom":subQ18}),-1.0]])]})]);}
            var Q1;
            Q1=makeQuery(id+"F5.boolean.opBoolean","SPLIT",FACE,{"disambiguationData":[TD([makeQuery(id+"F5.opExtrude","SWEPT_FACE",FACE,{"disambiguationData":[OSD([sQuery(id+"F4.wireOp",EDGE,"E41")])]})])],"derivedFrom":makeQuery(id+"F3.boolean.opBoolean","COPY",FACE,{"derivedFrom":makeQuery(id+"F3.opExtrude","CAP_FACE",FACE,{"disambiguationData":[OSD([sQuery(id+"F0.wireOp",EDGE,"E25.0"),sQuery(id+"F0.wireOp",EDGE,"E25.1"),sQuery(id+"F0.wireOp",EDGE,"E25.2"),sQuery(id+"F0.wireOp",EDGE,"E25.3"),sQuery(id+"F0.wireOp",EDGE,"E25.4"),sQuery(id+"F0.wireOp",EDGE,"E25.5"),sQuery(id+"F0.wireOp",EDGE,"E25.6"),sQuery(id+"F0.wireOp",EDGE,"E25.7")])],"isStart":false})})});
            extrude(context, id + "F13", {"entities" : qUnion([Q0]), "operationType" : NewBodyOperationType.REMOVE, "endBound" : BoundingType.UP_TO_SURFACE, "endBoundEntityFace" : qUnion([Q1]), "depth" : 25 * mm});
        }
        {
            var Q0;
            Q0=makeQuery(id+"F3.boolean.opBoolean","COPY",EDGE,{"derivedFrom":makeQuery(id+"F3.opExtrude","CAP_EDGE",EDGE,{"disambiguationData":[OSD([sQuery(id+"F0.wireOp",EDGE,"E25.6")])],"isStart":false})});
            var Q1;
            Q1=makeQuery(id+"F8.boolean.opBoolean","INTERSECT",EDGE,{"derivedFrom":[makeQuery(id+"F5.opExtrude","SWEPT_FACE",FACE,{"disambiguationData":[OSD([sQuery(id+"F4.wireOp",EDGE,"E30")])]}),makeQuery(id+"F8.opExtrude","CAP_FACE",FACE,{"disambiguationData":[OSD([sQuery(id+"F7.wireOp",EDGE,"E67")])],"isStart":false})]});
            var Q2;
            Q2=makeQuery(id+"F8.boolean.opBoolean","INTERSECT",EDGE,{"disambiguationData":[OD(1.0)],"derivedFrom":[makeQuery(id+"F5.opExtrude","SWEPT_FACE",FACE,{"disambiguationData":[OSD([sQuery(id+"F4.wireOp",EDGE,"E30")])]}),makeQuery(id+"F8.opExtrude","SWEPT_FACE",FACE,{"disambiguationData":[OSD([sQuery(id+"F7.wireOp",EDGE,"E67")])]})]});
            var Q3;
            {var subQ0=sQuery(id+"F4.wireOp",EDGE,"E30");Q3=makeQuery(id+"F8.boolean.opBoolean","SPLIT",EDGE,{"disambiguationData":[TD([makeQuery(id+"F5.opExtrude","SWEPT_FACE",FACE,{"disambiguationData":[OSD([sQuery(id+"F4.wireOp",EDGE,"E35.filletArc")])]})])],"derivedFrom":makeQuery(id+"F5.opExtrude","CAP_EDGE",EDGE,{"disambiguationData":[OSD([subQ0])],"isStart":false})});}
            var Q4;
            {var subQ0=sQuery(id+"F0.wireOp",EDGE,"E25.7");var subQ1=sQuery(id+"F0.wireOp",EDGE,"E25.1");var subQ2=sQuery(id+"F0.wireOp",EDGE,"E25.6");var subQ3=sQuery(id+"F0.wireOp",EDGE,"E25.5");var subQ4=sQuery(id+"F0.wireOp",EDGE,"E25.4");var subQ5=sQuery(id+"F0.wireOp",EDGE,"E25.0");var subQ6=sQuery(id+"F0.wireOp",EDGE,"E25.2");var subQ7=sQuery(id+"F0.wireOp",EDGE,"E25.3");Q4=makeQuery(id+"F8.boolean.opBoolean","INTERSECT",EDGE,{"derivedFrom":[makeQuery(id+"F5.boolean.opBoolean","SPLIT",FACE,{"disambiguationData":[TD([makeQuery(id+"F2.opExtrude","SWEPT_FACE",FACE,{"disambiguationData":[OSD([subQ5])]})])],"derivedFrom":makeQuery(id+"F3.boolean.opBoolean","COPY",FACE,{"derivedFrom":makeQuery(id+"F3.opExtrude","CAP_FACE",FACE,{"disambiguationData":[OSD([subQ5,subQ1,subQ6,subQ7,subQ4,subQ3,subQ2,subQ0])],"isStart":false})})}),makeQuery(id+"F8.opExtrude","SWEPT_FACE",FACE,{"disambiguationData":[OSD([sQuery(id+"F7.wireOp",EDGE,"E67")])]})]});}
            var Q5;
            Q5=makeQuery(id+"F8.boolean.opBoolean","INTERSECT",EDGE,{"disambiguationData":[OD(0.0)],"derivedFrom":[makeQuery(id+"F5.opExtrude","SWEPT_FACE",FACE,{"disambiguationData":[OSD([sQuery(id+"F4.wireOp",EDGE,"E30")])]}),makeQuery(id+"F8.opExtrude","SWEPT_FACE",FACE,{"disambiguationData":[OSD([sQuery(id+"F7.wireOp",EDGE,"E67")])]})]});
            fillet(context, id + "F14", {"entities" : qUnion([Q0, Q1, Q2, Q3, Q4, Q5]), "radius" : 3 * mm, "tangentPropagation" : true, "allowEdgeOverflow" : false});
        }
        {
            var Q0;
            Q0=makeQuery(id+"F1.opExtrude","CAP_EDGE",EDGE,{"disambiguationData":[OSD([sQuery(id+"F0.wireOp",EDGE,"E1.bottom")])],"isStart":false});
            fillet(context, id + "F15", {"entities" : qUnion([Q0]), "radius" : 2 * mm, "tangentPropagation" : true, "allowEdgeOverflow" : false});
        }
        {
            var Q0;
            {var subQ0=sQuery(id+"F0.wireOp",EDGE,"E22.filletArc");var subQ1=sQuery(id+"F0.wireOp",EDGE,"E7");var subQ2=sQuery(id+"F0.wireOp",EDGE,"E6");var subQ3=sQuery(id+"F0.wireOp",EDGE,"E5");var subQ4=sQuery(id+"F0.wireOp",EDGE,"E4");var subQ5=sQuery(id+"F0.wireOp",EDGE,"E1.bottom");var subQ6=sQuery(id+"F0.wireOp",EDGE,"E21.filletArc");var subQ7=sQuery(id+"F0.wireOp",EDGE,"E1.top");var subQ8=sQuery(id+"F0.wireOp",EDGE,"E1.left");var subQ9=sQuery(id+"F0.wireOp",EDGE,"E1.right");var subQ10=sQuery(id+"F0.wireOp",EDGE,"E23.filletArc");var subQ11=sQuery(id+"F0.wireOp",EDGE,"E24.filletArc");Q0=makeQuery(id+"F2.boolean.opBoolean","SPLIT",FACE,{"disambiguationData":[TD([makeQuery(id+"F1.opExtrude","SWEPT_FACE",FACE,{"disambiguationData":[OSD([subQ5])]})])],"derivedFrom":makeQuery(id+"F1.opExtrude","CAP_FACE",FACE,{"disambiguationData":[OSD([subQ5,subQ7,subQ8,subQ9,subQ4,subQ3,subQ2,subQ1,subQ6,subQ0,subQ10,subQ11])],"isStart":true})});}
            var sketch = newSketch(context, id + "F16", { "sketchPlane" : qUnion([Q0])});
            skLineSegment(sketch, "E79", {"start": v(-42.83, 74.25) * mm, "end": v(-24.83, 92.25) * mm});
            skLineSegment(sketch, "E80", {"start": v(-24.83, 104.25) * mm, "end": v(-24.83, 92.25) * mm});
            skLineSegment(sketch, "E81", {"start": v(23.17, 74.25) * mm, "end": v(5.17, 92.25) * mm});
            skLineSegment(sketch, "E82", {"start": v(5.17, 92.25) * mm, "end": v(5.17, 104.25) * mm});
            skLineSegment(sketch, "E83", {"start": v(-42.83, 74.25) * mm, "end": v(23.17, 74.25) * mm});
            skArc(sketch, "E84", {"start": v(5.17, 104.25) * mm, "mid": v(-9.83, 119.25) * mm, "end": v(-24.83, 104.25) * mm});
            skCircle(sketch, "E85", {"center": v(-9.83, 104.25) * mm, "radius": 6 * mm});
            skLineSegment(sketch, "E86", {"start": v(-9.83, 104.25) * mm, "end": v(-9.83, 74.25) * mm});
            skLineSegment(sketch, "E87", {"start": v(-74.25, 0) * mm, "end": v(74.25, 0) * mm});
            skCircle(sketch, "E88.MirrorC", {"center": v(-9.83, -104.25) * mm, "radius": 6 * mm});
            skArc(sketch, "E89.MirrorCS", {"start": v(5.17, -104.25) * mm, "mid": v(-9.83, -119.25) * mm, "end": v(-24.83, -104.25) * mm});
            skLineSegment(sketch, "E90.MirrorCS", {"start": v(-42.83, -74.25) * mm, "end": v(23.17, -74.25) * mm});
            skLineSegment(sketch, "E91.MirrorCS", {"start": v(-42.83, -74.25) * mm, "end": v(-24.83, -92.25) * mm});
            skLineSegment(sketch, "E92.MirrorCS", {"start": v(-24.83, -104.25) * mm, "end": v(-24.83, -92.25) * mm});
            skLineSegment(sketch, "E93.MirrorCS", {"start": v(23.17, -74.25) * mm, "end": v(5.17, -92.25) * mm});
            skLineSegment(sketch, "E94.MirrorCS", {"start": v(5.17, -92.25) * mm, "end": v(5.17, -104.25) * mm});
            skLineSegment(sketch, "E95.MirrorCS", {"start": v(-9.83, -104.25) * mm, "end": v(-9.83, -74.25) * mm});
            skSolve(sketch);
        }
        {
            var Q0;
            Q0 = qSketchRegion(id + "F16", true);
            var Q1;
            {var subQ0=sQuery(id+"F4.wireOp",EDGE,"E36.filletArc");var subQ1=sQuery(id+"F4.wireOp",EDGE,"E35.filletArc");var subQ2=sQuery(id+"F4.wireOp",EDGE,"E34.filletArc");var subQ3=sQuery(id+"F4.wireOp",EDGE,"E33.filletArc");var subQ4=sQuery(id+"F4.wireOp",EDGE,"E27.0");var subQ5=sQuery(id+"F4.wireOp",EDGE,"E30");var subQ6=sQuery(id+"F4.wireOp",EDGE,"E28.0");var subQ7=sQuery(id+"F4.wireOp",EDGE,"E29");Q1=makeQuery(id+"F6.boolean.opBoolean","SPLIT",FACE,{"disambiguationData":[TD([makeQuery(id+"F5.opExtrude","SWEPT_FACE",FACE,{"disambiguationData":[OSD([subQ4])]})])],"derivedFrom":makeQuery(id+"F5.opExtrude","CAP_FACE",FACE,{"disambiguationData":[OSD([subQ4,subQ6,subQ7,subQ5,subQ3,subQ2,subQ1,subQ0,sQuery(id+"F4.wireOp",EDGE,"E41"),sQuery(id+"F4.wireOp",EDGE,"E42"),sQuery(id+"F4.wireOp",EDGE,"E43"),sQuery(id+"F4.wireOp",EDGE,"E45"),sQuery(id+"F4.wireOp",EDGE,"E46"),sQuery(id+"F4.wireOp",EDGE,"E47.filletArc"),sQuery(id+"F4.wireOp",EDGE,"E48.filletArc"),sQuery(id+"F4.wireOp",EDGE,"E49.filletArc"),sQuery(id+"F4.wireOp",EDGE,"E50.filletArc"),sQuery(id+"F4.wireOp",EDGE,"E51.filletArc"),sQuery(id+"F4.wireOp",EDGE,"E52.filletArc"),sQuery(id+"F4.wireOp",EDGE,"E53.0.MirrorCS"),sQuery(id+"F4.wireOp",EDGE,"E54.0.MirrorCS"),sQuery(id+"F4.wireOp",EDGE,"E55.0.MirrorCS"),sQuery(id+"F4.wireOp",EDGE,"E56.0.MirrorCS"),sQuery(id+"F4.wireOp",EDGE,"E57.0.MirrorCS"),sQuery(id+"F4.wireOp",EDGE,"E58.0.MirrorCS"),sQuery(id+"F4.wireOp",EDGE,"E59.0.MirrorCS"),sQuery(id+"F4.wireOp",EDGE,"E60.0.MirrorCS"),sQuery(id+"F4.wireOp",EDGE,"E61.0.MirrorCS"),sQuery(id+"F4.wireOp",EDGE,"E62.0.MirrorCS"),sQuery(id+"F4.wireOp",EDGE,"E63.0.MirrorCS")])],"isStart":true})});}
            var Q2;
            Q2=makeQuery(id+"F16.imprint","IMPRINT",FACE,{"disambiguationData":[TD([[makeQuery(id+"F16.imprint","IMPRINT",EDGE,{"derivedFrom":makeQuery(id+"F1.opExtrude","CAP_EDGE",EDGE,{"disambiguationData":[OSD([sQuery(id+"F0.wireOp",EDGE,"E6")])],"isStart":true})}),-1.0]])]});
            var Q3;
            Q3=makeQuery(id+"F16.imprint","IMPRINT",FACE,{"disambiguationData":[TD([[makeQuery(id+"F16.imprint","IMPRINT",EDGE,{"derivedFrom":makeQuery(id+"F1.opExtrude","CAP_EDGE",EDGE,{"disambiguationData":[OSD([sQuery(id+"F0.wireOp",EDGE,"E4")])],"isStart":true})}),-1.0]])]});
            extrude(context, id + "F17", {"entities" : qUnion([Q0, Q1, Q2, Q3]), "operationType" : NewBodyOperationType.ADD, "depth" : 2 * mm});
        }
        {
            var Q0;
            {var subQ4=sQuery(id+"F16.wireOp",EDGE,"E79");Q0=makeQuery(id+"F16.imprint","IMPRINT",FACE,{"disambiguationData":[TD([[makeQuery(id+"F16.imprint","IMPRINT",EDGE,{"derivedFrom":subQ4}),-1.0]])]});}
            var Q1;
            Q1=makeQuery(id+"F16.imprint","IMPRINT",FACE,{"disambiguationData":[TD([[makeQuery(id+"F16.imprint","IMPRINT",EDGE,{"derivedFrom":makeQuery(id+"F1.opExtrude","CAP_EDGE",EDGE,{"disambiguationData":[OSD([sQuery(id+"F0.wireOp",EDGE,"E4")])],"isStart":true})}),-1.0]])]});
            var Q2;
            Q2=makeQuery(id+"F16.imprint","IMPRINT",FACE,{"disambiguationData":[TD([[makeQuery(id+"F16.imprint","IMPRINT",EDGE,{"derivedFrom":makeQuery(id+"F1.opExtrude","CAP_EDGE",EDGE,{"disambiguationData":[OSD([sQuery(id+"F0.wireOp",EDGE,"E6")])],"isStart":true})}),-1.0]])]});
            var Q3;
            Q3=makeQuery(id+"F16.imprint","IMPRINT",FACE,{"disambiguationData":[TD([[makeQuery(id+"F16.imprint","IMPRINT",EDGE,{"derivedFrom":sQuery(id+"F16.wireOp",EDGE,"E88.MirrorC")}),1.0]])]});
            extrude(context, id + "F18", {"entities" : qUnion([Q0, Q1, Q2, Q3]), "depth" : 2 * mm});
        }
    });
